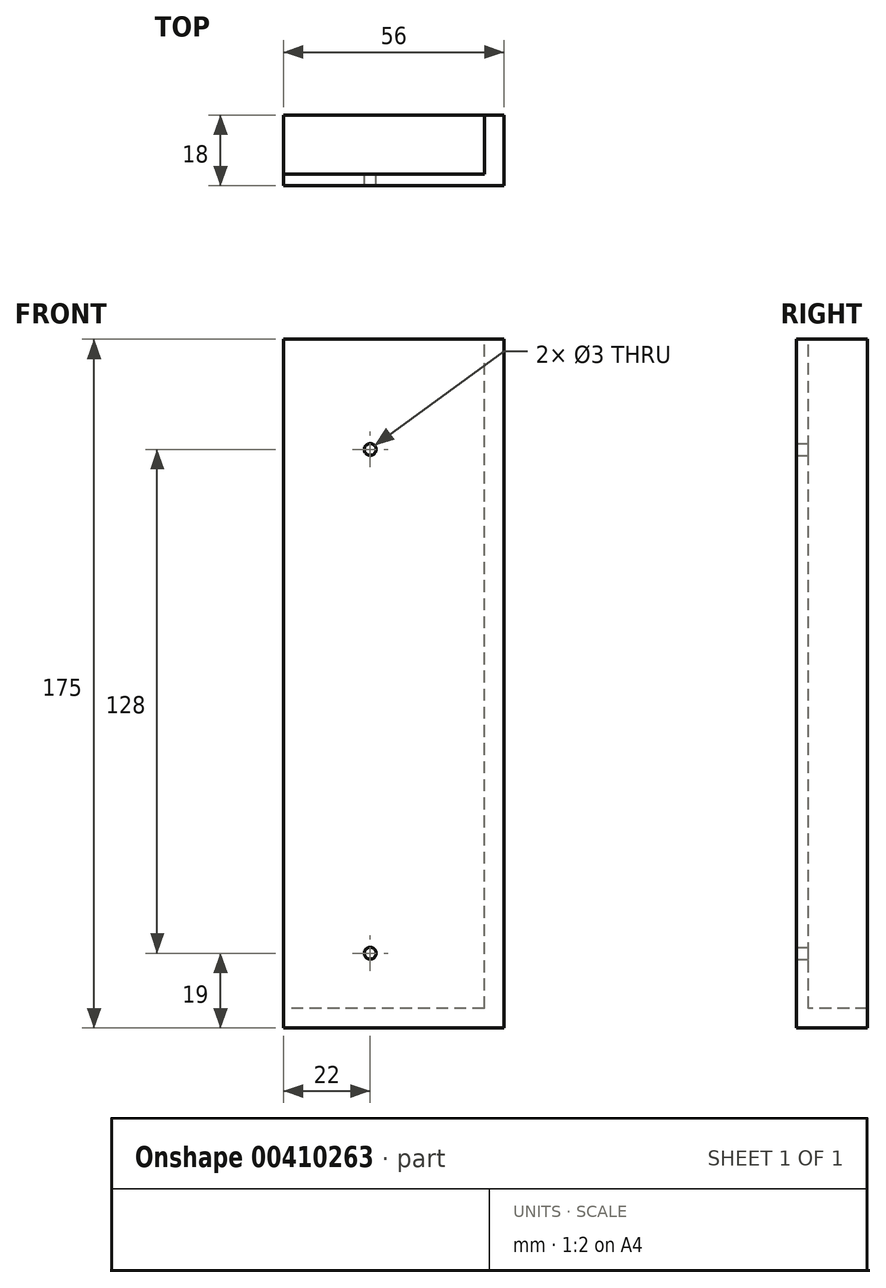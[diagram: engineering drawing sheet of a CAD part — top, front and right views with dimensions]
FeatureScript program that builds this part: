
annotation { "Feature Type Name" : "Feature", "Feature Type Description" : "" }
export const myFeature = defineFeature(function(context is Context, id is Id, definition is map)
    precondition{}
    {
        {
            var Q0;
            Q0=qCreatedBy(makeId("Front.planeOp"),FACE);
            var sketch = newSketch(context, id + "F0", { "sketchPlane" : qUnion([Q0])});
            skLineSegment(sketch, "E0.bottom", {"start": v(0, 0) * mm, "end": v(-51, 0) * mm});
            skLineSegment(sketch, "E0.top", {"start": v(0, 170) * mm, "end": v(-51, 170) * mm});
            skLineSegment(sketch, "E0.left", {"start": v(0, 0) * mm, "end": v(0, 170) * mm});
            skLineSegment(sketch, "E0.right", {"start": v(-51, 0) * mm, "end": v(-51, 170) * mm});
            skLineSegment(sketch, "E1", {"start": v(-7, 0) * mm, "end": v(-7, 170) * mm, "construction": true});
            skLineSegment(sketch, "E2", {"start": v(0, 9) * mm, "end": v(-51, 9) * mm, "construction": true});
            skLineSegment(sketch, "E3", {"start": v(-29, 170) * mm, "end": v(-29, 0) * mm, "construction": true});
            skCircle(sketch, "E4", {"center": v(-29, 14) * mm, "radius": 1.5 * mm});
            skCircle(sketch, "E5", {"center": v(-29, 142) * mm, "radius": 1.5 * mm});
            skLineSegment(sketch, "E6.bottom", {"start": v(0, 170) * mm, "end": v(5, 170) * mm});
            skLineSegment(sketch, "E6.top", {"start": v(0, -5) * mm, "end": v(5, -5) * mm});
            skLineSegment(sketch, "E6.left", {"start": v(0, 170) * mm, "end": v(0, 0) * mm});
            skLineSegment(sketch, "E6.right", {"start": v(5, 170) * mm, "end": v(5, -5) * mm});
            skLineSegment(sketch, "E7.bottom", {"start": v(0, -5) * mm, "end": v(-51, -5) * mm});
            skLineSegment(sketch, "E7.right", {"start": v(-51, -5) * mm, "end": v(-51, 0) * mm});
            skSolve(sketch);
        }
        {
            var Q0;
            Q0=makeQuery(id+"F0.imprint","IMPRINT",FACE,{"disambiguationData":[TD([[makeQuery(id+"F0.imprint","IMPRINT",EDGE,{"derivedFrom":sQuery(id+"F0.wireOp",EDGE,"E0.top")}),1.0]])]});
            extrude(context, id + "F1", {"entities" : qUnion([Q0]), "depth" : 3 * mm});
        }
        {
            var Q0;
            Q0=makeQuery(id+"F0.imprint","IMPRINT",FACE,{"disambiguationData":[TD([[makeQuery(id+"F0.imprint","IMPRINT",EDGE,{"derivedFrom":sQuery(id+"F0.wireOp",EDGE,"E6.bottom")}),-1.0]])]});
            extrude(context, id + "F2", {"entities" : qUnion([Q0]), "operationType" : NewBodyOperationType.ADD, "depth" : 3 * mm});
        }
        {
            var Q0;
            Q0=makeQuery(id+"F0.imprint","IMPRINT",FACE,{"disambiguationData":[TD([[makeQuery(id+"F0.imprint","IMPRINT",EDGE,{"derivedFrom":sQuery(id+"F0.wireOp",EDGE,"E6.bottom")}),-1.0]])]});
            extrude(context, id + "F3", {"entities" : qUnion([Q0]), "operationType" : NewBodyOperationType.ADD, "oppositeDirection" : true, "depth" : 15 * mm});
        }
    });
